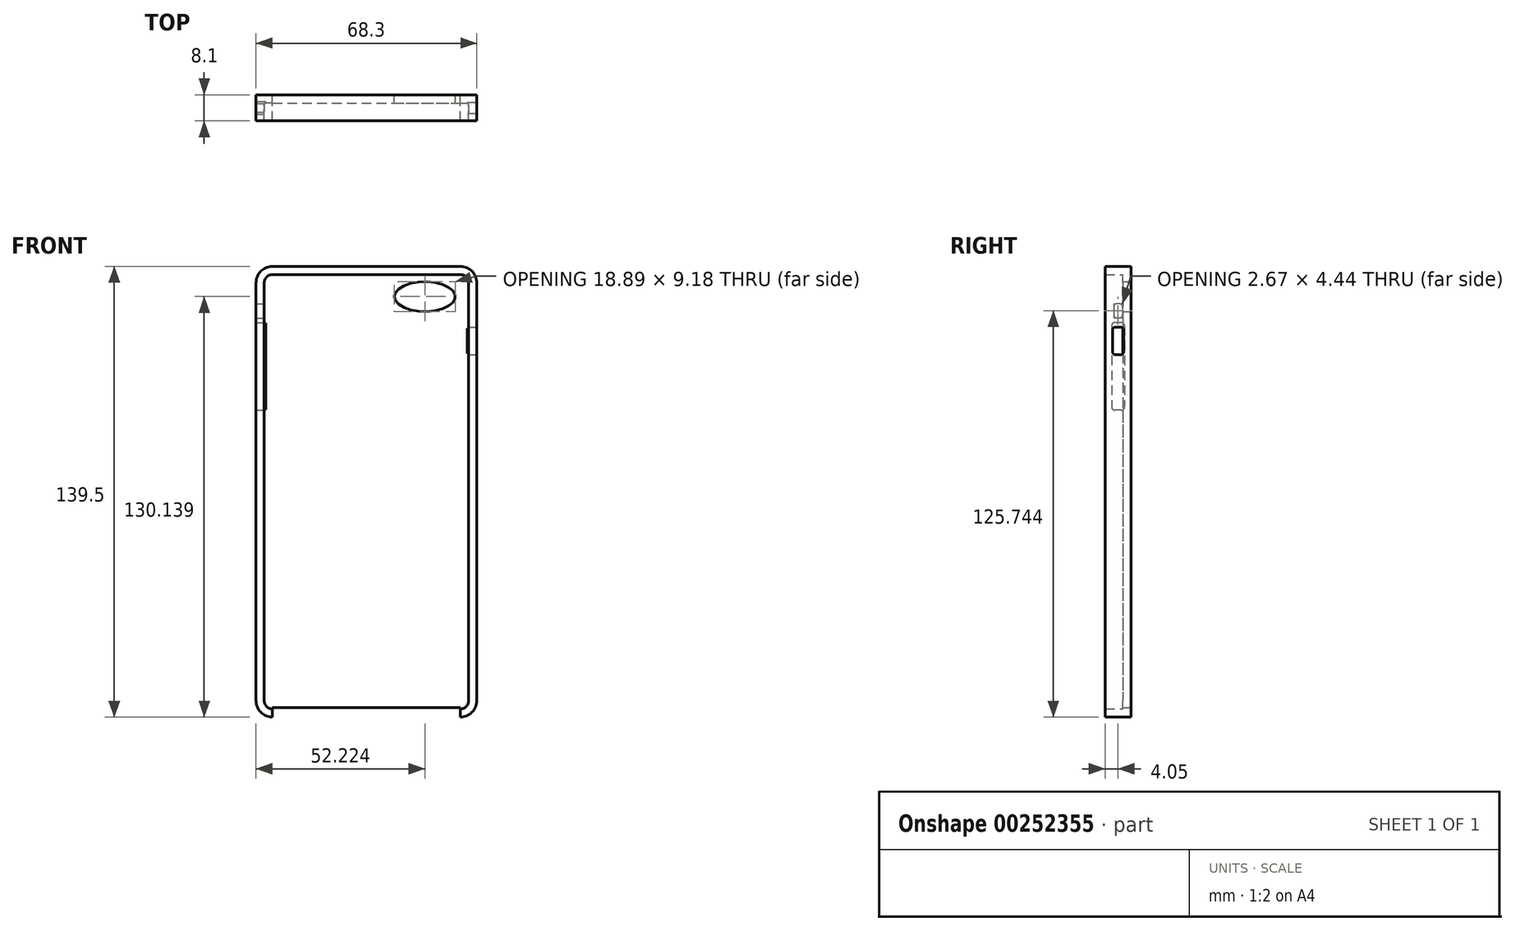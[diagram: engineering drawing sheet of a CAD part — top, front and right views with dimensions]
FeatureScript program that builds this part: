
annotation { "Feature Type Name" : "Feature", "Feature Type Description" : "" }
export const myFeature = defineFeature(function(context is Context, id is Id, definition is map)
    precondition{}
    {
        {
            var Q0;
            Q0=qCreatedBy(makeId("Front.planeOp"),FACE);
            var sketch = newSketch(context, id + "F0", { "sketchPlane" : qUnion([Q0])});
            skLineSegment(sketch, "E0.bottom", {"start": v(34.15, 69.75) * mm, "end": v(-34.15, 69.75) * mm});
            skLineSegment(sketch, "E0.top", {"start": v(34.15, -69.75) * mm, "end": v(-34.15, -69.75) * mm});
            skLineSegment(sketch, "E0.left", {"start": v(34.15, 69.75) * mm, "end": v(34.15, -69.75) * mm});
            skLineSegment(sketch, "E0.right", {"start": v(-34.15, 69.75) * mm, "end": v(-34.15, -69.75) * mm});
            skPoint(sketch, "E0.middle", {"position": v(0, 0) * mm});
            skSolve(sketch);
        }
        {
            var Q0;
            Q0=makeQuery(id+"F0.imprint","IMPRINT",FACE,{"disambiguationData":[TD([[makeQuery(id+"F0.imprint","IMPRINT",EDGE,{"derivedFrom":sQuery(id+"F0.wireOp",EDGE,"E0.bottom")}),1.0]])]});
            extrude(context, id + "F1", {"entities" : qUnion([Q0]), "endBound" : BoundingType.SYMMETRIC, "depth" : 8.1 * mm});
        }
        {
            var Q0;
            Q0=makeQuery(id+"F1.opExtrude","SWEPT_EDGE",EDGE,{"disambiguationData":[OSD([sQuery(id+"F0.wireOp",EDGE,"E0.bottom"),sQuery(id+"F0.wireOp",EDGE,"E0.right")])]});
            var Q1;
            Q1=makeQuery(id+"F1.opExtrude","SWEPT_EDGE",EDGE,{"disambiguationData":[OSD([sQuery(id+"F0.wireOp",EDGE,"E0.bottom"),sQuery(id+"F0.wireOp",EDGE,"E0.left")])]});
            var Q2;
            Q2=makeQuery(id+"F1.opExtrude","SWEPT_EDGE",EDGE,{"disambiguationData":[OSD([sQuery(id+"F0.wireOp",EDGE,"E0.top"),sQuery(id+"F0.wireOp",EDGE,"E0.left")])]});
            var Q3;
            Q3=makeQuery(id+"F1.opExtrude","SWEPT_EDGE",EDGE,{"disambiguationData":[OSD([sQuery(id+"F0.wireOp",EDGE,"E0.top"),sQuery(id+"F0.wireOp",EDGE,"E0.right")])]});
            fillet(context, id + "F2", {"entities" : qUnion([Q0, Q1, Q2, Q3]), "radius" : 5.08 * mm, "tangentPropagation" : true, "allowEdgeOverflow" : false});
        }
        {
            var Q0;
            Q0=makeQuery(id+"F1.opExtrude","CAP_FACE",FACE,{"disambiguationData":[OSD([sQuery(id+"F0.wireOp",EDGE,"E0.bottom"),sQuery(id+"F0.wireOp",EDGE,"E0.top"),sQuery(id+"F0.wireOp",EDGE,"E0.left"),sQuery(id+"F0.wireOp",EDGE,"E0.right")])],"isStart":false});
            var Q1;
            Q1=makeQuery(id+"F1.opExtrude","SWEPT_BODY",BODY,{"disambiguationData":[OSD([sQuery(id+"F0.wireOp",EDGE,"E0.bottom"),sQuery(id+"F0.wireOp",EDGE,"E0.top"),sQuery(id+"F0.wireOp",EDGE,"E0.left"),sQuery(id+"F0.wireOp",EDGE,"E0.right")])]});
            shell(context, id + "F3", {"entities" : qUnion([Q0]), "parts" : qUnion([Q1]), "thickness" : 2.54 * mm});
        }
        {
            var Q0;
            Q0=makeQuery(id+"F3.opShell","OFFSET_FACE",FACE,{"disambiguationData":[OSD([sQuery(id+"F0.wireOp",EDGE,"E0.bottom"),sQuery(id+"F0.wireOp",EDGE,"E0.top"),sQuery(id+"F0.wireOp",EDGE,"E0.left"),sQuery(id+"F0.wireOp",EDGE,"E0.right")])]});
            var sketch = newSketch(context, id + "F4", { "sketchPlane" : qUnion([Q0])});
            skEllipse(sketch, "E1", {"center": v(18.07, 60.39) * mm, "majorRadius": 9.45 * mm, "minorRadius": 4.59 * mm, "majorAxis": v(-1, 0)});
            skSolve(sketch);
        }
        {
            var Q0;
            Q0=makeQuery(id+"F4.imprint","IMPRINT",FACE,{"disambiguationData":[TD([[makeQuery(id+"F4.imprint","IMPRINT",EDGE,{"derivedFrom":sQuery(id+"F4.wireOp",EDGE,"E1")}),1.0]])]});
            extrude(context, id + "F5", {"entities" : qUnion([Q0]), "operationType" : NewBodyOperationType.REMOVE, "endBound" : BoundingType.SYMMETRIC, "depth" : 60 * mm});
        }
        {
            var Q0;
            Q0=makeQuery(id+"F1.opExtrude","SWEPT_FACE",FACE,{"disambiguationData":[OSD([sQuery(id+"F0.wireOp",EDGE,"E0.right")])]});
            var sketch = newSketch(context, id + "F6", { "sketchPlane" : qUnion([Q0])});
            skSolve(sketch);
        }
        {
            var Q0;
            Q0=makeQuery(id+"F1.opExtrude","SWEPT_FACE",FACE,{"disambiguationData":[OSD([sQuery(id+"F0.wireOp",EDGE,"E0.top")])]});
            var sketch = newSketch(context, id + "F7", { "sketchPlane" : qUnion([Q0])});
            skLineSegment(sketch, "E2", {"start": v(-12.62, -4.05) * mm, "end": v(19.5, -4.05) * mm});
            skLineSegment(sketch, "E3", {"start": v(19.5, -4.05) * mm, "end": v(19.5, 4.05) * mm});
            skLineSegment(sketch, "E4", {"start": v(19.5, 4.05) * mm, "end": v(-12.62, 4.05) * mm});
            skLineSegment(sketch, "E5", {"start": v(-12.62, 4.05) * mm, "end": v(-12.62, -4.05) * mm});
            skSolve(sketch);
        }
        {
            var Q0;
            Q0=makeQuery(id+"F7.imprint","IMPRINT",FACE,{"disambiguationData":[TD([[makeQuery(id+"F7.imprint","IMPRINT",EDGE,{"derivedFrom":sQuery(id+"F7.wireOp",EDGE,"E2")}),-1.0]])]});
            extrude(context, id + "F8", {"entities" : qUnion([Q0]), "operationType" : NewBodyOperationType.REMOVE, "endBound" : BoundingType.SYMMETRIC, "oppositeDirection" : true, "depth" : 6 * mm});
        }
        {
            var Q0;
            Q0=makeQuery(id+"F1.opExtrude","SWEPT_FACE",FACE,{"disambiguationData":[OSD([sQuery(id+"F0.wireOp",EDGE,"E0.left")])]});
            var sketch = newSketch(context, id + "F9", { "sketchPlane" : qUnion([Q0])});
            skLineSegment(sketch, "E6.bottom", {"start": v(1.72, 42.37) * mm, "end": v(-1.72, 42.37) * mm});
            skLineSegment(sketch, "E6.top", {"start": v(1.72, 50.97) * mm, "end": v(-1.72, 50.97) * mm});
            skLineSegment(sketch, "E6.left", {"start": v(1.72, 42.37) * mm, "end": v(1.72, 50.97) * mm});
            skLineSegment(sketch, "E6.right", {"start": v(-1.72, 42.37) * mm, "end": v(-1.72, 50.97) * mm});
            skPoint(sketch, "E6.middle", {"position": v(0, 46.67) * mm});
            skSolve(sketch);
        }
        {
            var Q0;
            Q0=makeQuery(id+"F9.imprint","IMPRINT",FACE,{"disambiguationData":[TD([[makeQuery(id+"F9.imprint","IMPRINT",EDGE,{"derivedFrom":sQuery(id+"F9.wireOp",EDGE,"E6.bottom")}),-1.0]])]});
            extrude(context, id + "F10", {"entities" : qUnion([Q0]), "operationType" : NewBodyOperationType.REMOVE, "endBound" : BoundingType.SYMMETRIC, "oppositeDirection" : true, "depth" : 6 * mm});
        }
        {
            var Q0;
            {var subQ0=sQuery(id+"F0.wireOp",EDGE,"E0.right");Q0=makeQuery(id+"F6.imprint","IMPRINT",FACE,{"disambiguationData":[TD([[makeQuery(id+"F6.imprint","IMPRINT",EDGE,{"derivedFrom":makeQuery(id+"F1.opExtrude","CAP_EDGE",EDGE,{"disambiguationData":[OSD([subQ0])],"isStart":true})}),1.0]])]});}
            var sketch = newSketch(context, id + "F11", { "sketchPlane" : qUnion([Q0])});
            skLineSegment(sketch, "E7.bottom", {"start": v(-1.33, 58.21) * mm, "end": v(1.33, 58.21) * mm});
            skLineSegment(sketch, "E7.top", {"start": v(-1.33, 53.78) * mm, "end": v(1.33, 53.78) * mm});
            skLineSegment(sketch, "E7.left", {"start": v(-1.33, 58.21) * mm, "end": v(-1.33, 53.78) * mm});
            skLineSegment(sketch, "E7.right", {"start": v(1.33, 58.21) * mm, "end": v(1.33, 53.78) * mm});
            skPoint(sketch, "E7.middle", {"position": v(0, 56) * mm});
            skSolve(sketch);
        }
        {
            var Q0;
            Q0=qSketchRegion(id+"F11",true);
            extrude(context, id + "F12", {"entities" : qUnion([Q0]), "operationType" : NewBodyOperationType.REMOVE, "endBound" : BoundingType.SYMMETRIC, "depth" : 6 * mm});
        }
        {
            var Q0;
            {var subQ0=sQuery(id+"F0.wireOp",EDGE,"E0.right");Q0=makeQuery(id+"F6.imprint","IMPRINT",FACE,{"disambiguationData":[TD([[makeQuery(id+"F6.imprint","IMPRINT",EDGE,{"derivedFrom":makeQuery(id+"F1.opExtrude","CAP_EDGE",EDGE,{"disambiguationData":[OSD([subQ0])],"isStart":true})}),1.0]])]});}
            var sketch = newSketch(context, id + "F13", { "sketchPlane" : qUnion([Q0])});
            skLineSegment(sketch, "E8.bottom", {"start": v(-2.02, 52.3) * mm, "end": v(2.02, 52.3) * mm});
            skLineSegment(sketch, "E8.top", {"start": v(-2.02, 25.26) * mm, "end": v(2.02, 25.26) * mm});
            skLineSegment(sketch, "E8.left", {"start": v(-2.02, 52.3) * mm, "end": v(-2.02, 25.26) * mm});
            skLineSegment(sketch, "E8.right", {"start": v(2.02, 52.3) * mm, "end": v(2.02, 25.26) * mm});
            skPoint(sketch, "E8.middle", {"position": v(0, 38.78) * mm});
            skSolve(sketch);
        }
        {
            var Q0;
            Q0=qSketchRegion(id+"F13",true);
            extrude(context, id + "F14", {"entities" : qUnion([Q0]), "operationType" : NewBodyOperationType.REMOVE, "endBound" : BoundingType.SYMMETRIC, "depth" : 6 * mm});
        }
        {
            var Q0;
            {var subQ2=sQuery(id+"F0.wireOp",EDGE,"E0.top");Q0=makeQuery(id+"F8.boolean.opBoolean","SPLIT",FACE,{"disambiguationData":[TD([makeQuery(id+"F8.opExtrude","SWEPT_FACE",FACE,{"disambiguationData":[OSD([sQuery(id+"F7.wireOp",EDGE,"E5")])]})])],"derivedFrom":makeQuery(id+"F1.opExtrude","SWEPT_FACE",FACE,{"disambiguationData":[OSD([subQ2])]})});}
            var sketch = newSketch(context, id + "F15", { "sketchPlane" : qUnion([Q0])});
            skSolve(sketch);
        }
        {
            var Q0;
            {var subQ0=sQuery(id+"F0.wireOp",EDGE,"E0.top");var subQ1=makeQuery(id+"F1.opExtrude","SWEPT_FACE",FACE,{"disambiguationData":[OSD([subQ0])]});var subQ6=makeQuery(id+"F8.opExtrude","SWEPT_FACE",FACE,{"disambiguationData":[OSD([sQuery(id+"F7.wireOp",EDGE,"E5")])]});Q0=makeQuery(id+"F15.imprint","IMPRINT",FACE,{"disambiguationData":[TD([[makeQuery(id+"F15.imprint","IMPRINT",EDGE,{"derivedFrom":makeQuery(id+"F8.boolean.opBoolean","INTERSECT",EDGE,{"derivedFrom":[subQ1,subQ6]})}),-1.0]])]});}
            var Q1;
            {var subQ2=sQuery(id+"F0.wireOp",EDGE,"E0.top");Q1=makeQuery(id+"F8.boolean.opBoolean","SPLIT",FACE,{"disambiguationData":[TD([makeQuery(id+"F8.opExtrude","SWEPT_FACE",FACE,{"disambiguationData":[OSD([sQuery(id+"F7.wireOp",EDGE,"E3")])]})])],"derivedFrom":makeQuery(id+"F1.opExtrude","SWEPT_FACE",FACE,{"disambiguationData":[OSD([subQ2])]})});}
            extrude(context, id + "F16", {"entities" : qUnion([Q0, Q1]), "operationType" : NewBodyOperationType.REMOVE, "oppositeDirection" : true, "depth" : 3 * mm});
        }
        {
            var Q0;
            Q0=makeQuery(id+"F10.boolean.opBoolean","COPY",EDGE,{"derivedFrom":makeQuery(id+"F10.opExtrude","SWEPT_EDGE",EDGE,{"disambiguationData":[OSD([sQuery(id+"F9.wireOp",EDGE,"E6.bottom"),sQuery(id+"F9.wireOp",EDGE,"E6.right")])]})});
            var Q1;
            Q1=makeQuery(id+"F10.boolean.opBoolean","COPY",EDGE,{"derivedFrom":makeQuery(id+"F10.opExtrude","SWEPT_EDGE",EDGE,{"disambiguationData":[OSD([sQuery(id+"F9.wireOp",EDGE,"E6.top"),sQuery(id+"F9.wireOp",EDGE,"E6.right")])]})});
            var Q2;
            Q2=makeQuery(id+"F10.boolean.opBoolean","COPY",EDGE,{"derivedFrom":makeQuery(id+"F10.opExtrude","SWEPT_EDGE",EDGE,{"disambiguationData":[OSD([sQuery(id+"F9.wireOp",EDGE,"E6.bottom"),sQuery(id+"F9.wireOp",EDGE,"E6.left")])]})});
            var Q3;
            Q3=makeQuery(id+"F10.boolean.opBoolean","COPY",EDGE,{"derivedFrom":makeQuery(id+"F10.opExtrude","SWEPT_EDGE",EDGE,{"disambiguationData":[OSD([sQuery(id+"F9.wireOp",EDGE,"E6.top"),sQuery(id+"F9.wireOp",EDGE,"E6.left")])]})});
            fillet(context, id + "F17", {"entities" : qUnion([Q0, Q1, Q2, Q3]), "radius" : 1 * mm, "tangentPropagation" : true, "allowEdgeOverflow" : false});
        }
        {
            var Q0;
            Q0=makeQuery(id+"F14.boolean.opBoolean","COPY",EDGE,{"derivedFrom":makeQuery(id+"F14.opExtrude","SWEPT_EDGE",EDGE,{"disambiguationData":[OSD([sQuery(id+"F13.wireOp",EDGE,"E8.top"),sQuery(id+"F13.wireOp",EDGE,"E8.left")])]})});
            var Q1;
            Q1=makeQuery(id+"F14.boolean.opBoolean","COPY",EDGE,{"derivedFrom":makeQuery(id+"F14.opExtrude","SWEPT_EDGE",EDGE,{"disambiguationData":[OSD([sQuery(id+"F13.wireOp",EDGE,"E8.top"),sQuery(id+"F13.wireOp",EDGE,"E8.right")])]})});
            var Q2;
            Q2=makeQuery(id+"F14.boolean.opBoolean","COPY",EDGE,{"derivedFrom":makeQuery(id+"F14.opExtrude","SWEPT_EDGE",EDGE,{"disambiguationData":[OSD([sQuery(id+"F13.wireOp",EDGE,"E8.bottom"),sQuery(id+"F13.wireOp",EDGE,"E8.right")])]})});
            var Q3;
            Q3=makeQuery(id+"F14.boolean.opBoolean","COPY",EDGE,{"derivedFrom":makeQuery(id+"F14.opExtrude","SWEPT_EDGE",EDGE,{"disambiguationData":[OSD([sQuery(id+"F13.wireOp",EDGE,"E8.bottom"),sQuery(id+"F13.wireOp",EDGE,"E8.left")])]})});
            fillet(context, id + "F18", {"entities" : qUnion([Q0, Q1, Q2, Q3]), "radius" : 1 * mm, "tangentPropagation" : true, "allowEdgeOverflow" : false});
        }
        {
            var Q0;
            Q0=makeQuery(id+"F12.boolean.opBoolean","COPY",EDGE,{"derivedFrom":makeQuery(id+"F12.opExtrude","SWEPT_EDGE",EDGE,{"disambiguationData":[OSD([sQuery(id+"F11.wireOp",EDGE,"E7.bottom"),sQuery(id+"F11.wireOp",EDGE,"E7.left")])]})});
            var Q1;
            Q1=makeQuery(id+"F12.boolean.opBoolean","COPY",EDGE,{"derivedFrom":makeQuery(id+"F12.opExtrude","SWEPT_EDGE",EDGE,{"disambiguationData":[OSD([sQuery(id+"F11.wireOp",EDGE,"E7.top"),sQuery(id+"F11.wireOp",EDGE,"E7.left")])]})});
            var Q2;
            Q2=makeQuery(id+"F12.boolean.opBoolean","COPY",EDGE,{"derivedFrom":makeQuery(id+"F12.opExtrude","SWEPT_EDGE",EDGE,{"disambiguationData":[OSD([sQuery(id+"F11.wireOp",EDGE,"E7.top"),sQuery(id+"F11.wireOp",EDGE,"E7.right")])]})});
            var Q3;
            Q3=makeQuery(id+"F12.boolean.opBoolean","COPY",EDGE,{"derivedFrom":makeQuery(id+"F12.opExtrude","SWEPT_EDGE",EDGE,{"disambiguationData":[OSD([sQuery(id+"F11.wireOp",EDGE,"E7.bottom"),sQuery(id+"F11.wireOp",EDGE,"E7.right")])]})});
            fillet(context, id + "F19", {"entities" : qUnion([Q0, Q1, Q2, Q3]), "radius" : 1 * mm, "tangentPropagation" : true, "allowEdgeOverflow" : false});
        }
    });
